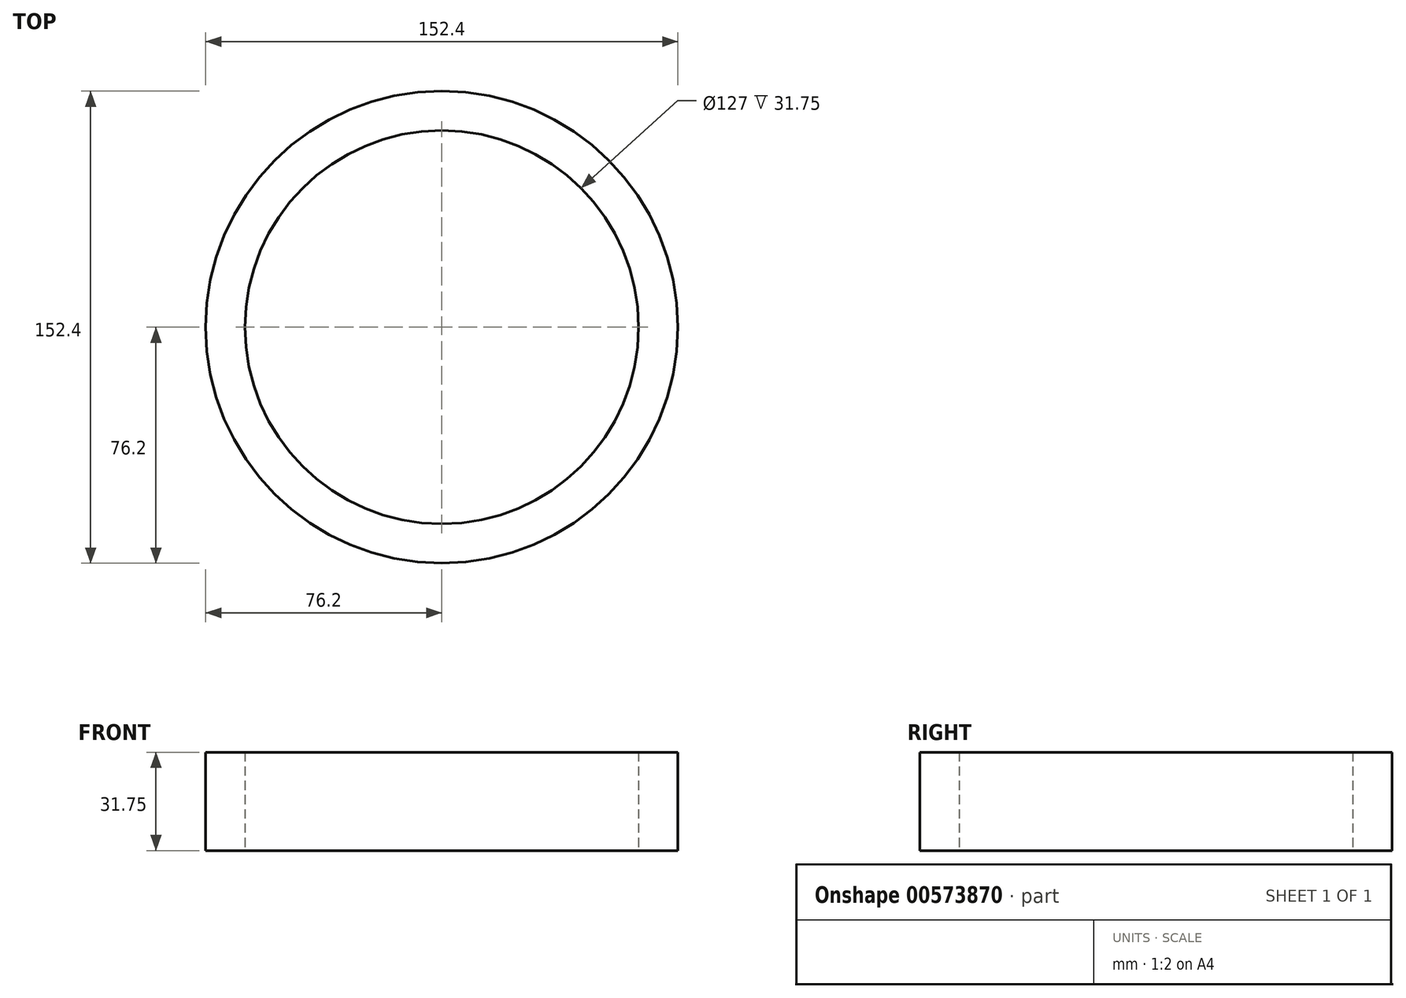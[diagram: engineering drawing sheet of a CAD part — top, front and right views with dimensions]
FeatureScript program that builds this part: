
annotation { "Feature Type Name" : "Feature", "Feature Type Description" : "" }
export const myFeature = defineFeature(function(context is Context, id is Id, definition is map)
    precondition{}
    {
        {
            var Q0;
            Q0=qCreatedBy(makeId("Top.planeOp"),FACE);
            var sketch = newSketch(context, id + "F0", { "sketchPlane" : qUnion([Q0])});
            skCircle(sketch, "E0", {"center": v(0, 0) * mm, "radius": 76.2 * mm});
            skCircle(sketch, "E1", {"center": v(0, 0) * mm, "radius": 63.5 * mm});
            skSolve(sketch);
        }
        {
            var Q0;
            Q0 = qSketchRegion(id + "F0", true);
            extrude(context, id + "F1", {"entities" : qUnion([Q0]), "depth" : 31.75 * mm, "offsetDistance" : 25.4 * mm});
        }
    });
